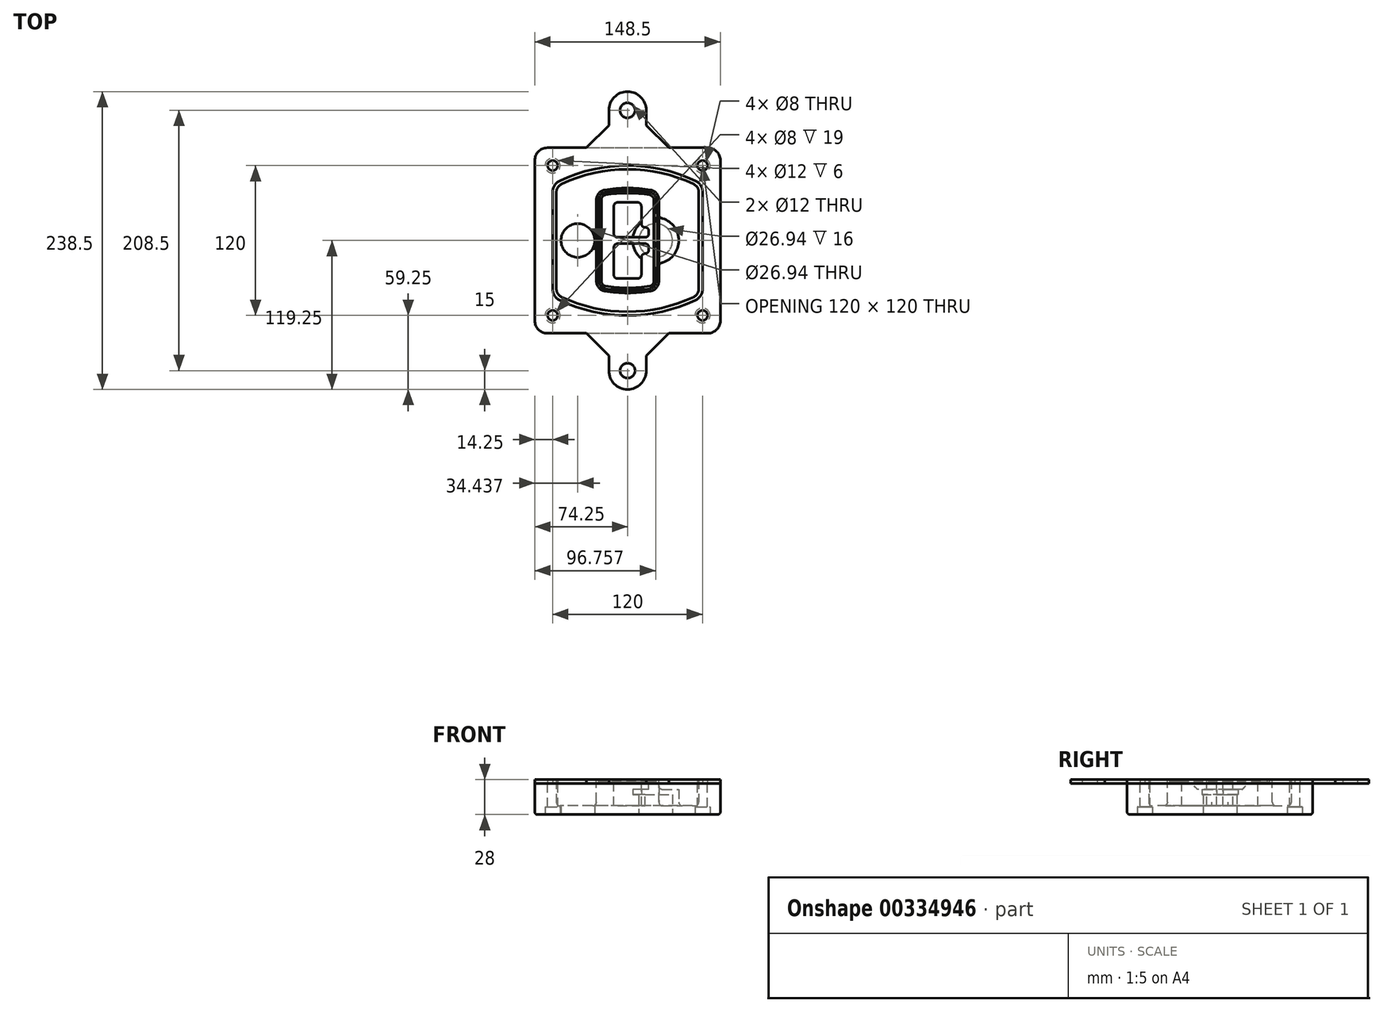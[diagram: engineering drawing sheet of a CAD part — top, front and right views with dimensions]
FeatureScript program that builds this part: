
annotation { "Feature Type Name" : "Feature", "Feature Type Description" : "" }
export const myFeature = defineFeature(function(context is Context, id is Id, definition is map)
    precondition{}
    {
        {
            var Q0;
            Q0=qCreatedBy(makeId("Top.planeOp"),FACE);
            var sketch = newSketch(context, id + "F0", { "sketchPlane" : qUnion([Q0])});
            skPoint(sketch, "E0.rect.middle", {"position": v(0, 0) * mm});
            skLineSegment(sketch, "E1.bottom", {"start": v(-64.25, -74.25) * mm, "end": v(64.25, -74.25) * mm});
            skLineSegment(sketch, "E1.top", {"start": v(-64.25, 74.25) * mm, "end": v(64.25, 74.25) * mm});
            skLineSegment(sketch, "E1.left", {"start": v(-74.25, -64.25) * mm, "end": v(-74.25, 64.25) * mm});
            skLineSegment(sketch, "E1.right", {"start": v(74.25, -64.25) * mm, "end": v(74.25, 64.25) * mm});
            skLineSegment(sketch, "E2", {"start": v(-74.25, 74.25) * mm, "end": v(74.25, -74.25) * mm, "construction": true});
            skLineSegment(sketch, "E3", {"start": v(74.25, 74.25) * mm, "end": v(-74.25, -74.25) * mm, "construction": true});
            skCircle(sketch, "E4", {"center": v(-60, 60) * mm, "radius": 4 * mm});
            skCircle(sketch, "E5", {"center": v(60, 60) * mm, "radius": 4 * mm});
            skCircle(sketch, "E6", {"center": v(60, -60) * mm, "radius": 4 * mm});
            skCircle(sketch, "E7", {"center": v(-60, -60) * mm, "radius": 4 * mm});
            skLineSegment(sketch, "E8", {"start": v(-60, 60) * mm, "end": v(60, 60) * mm, "construction": true});
            skLineSegment(sketch, "E9", {"start": v(60, 60) * mm, "end": v(60, -60) * mm, "construction": true});
            skLineSegment(sketch, "E10", {"start": v(60, -60) * mm, "end": v(-60, -60) * mm, "construction": true});
            skLineSegment(sketch, "E11", {"start": v(-60, -60) * mm, "end": v(-60, 60) * mm, "construction": true});
            skLineSegment(sketch, "E12", {"start": v(-60, 38.83) * mm, "end": v(-60, -38.83) * mm});
            skLineSegment(sketch, "E13", {"start": v(60, 38.83) * mm, "end": v(60, -38.83) * mm});
            skArc(sketch, "E14", {"start": v(54.26, 47.88) * mm, "mid": v(0, 60) * mm, "end": v(-54.26, 47.88) * mm});
            skArc(sketch, "E15", {"start": v(-54.26, -47.88) * mm, "mid": v(0, -60) * mm, "end": v(54.26, -47.88) * mm});
            skLineSegment(sketch, "E16", {"start": v(-60, 0) * mm, "end": v(60, 0) * mm, "construction": true});
            skPoint(sketch, "E17.visualSharp", {"position": v(-60, -45) * mm});
            skArc(sketch, "E17.filletArc", {"start": v(-60, -38.83) * mm, "mid": v(-58.44, -44.2) * mm, "end": v(-54.26, -47.88) * mm});
            skPoint(sketch, "E18.visualSharp", {"position": v(-60, 45) * mm});
            skArc(sketch, "E18.filletArc", {"start": v(-54.26, 47.88) * mm, "mid": v(-58.44, 44.2) * mm, "end": v(-60, 38.83) * mm});
            skPoint(sketch, "E19.visualSharp", {"position": v(60, 45) * mm});
            skArc(sketch, "E19.filletArc", {"start": v(60, 38.83) * mm, "mid": v(58.44, 44.2) * mm, "end": v(54.26, 47.88) * mm});
            skPoint(sketch, "E20.visualSharp", {"position": v(60, -45) * mm});
            skArc(sketch, "E20.filletArc", {"start": v(54.26, -47.88) * mm, "mid": v(58.44, -44.2) * mm, "end": v(60, -38.83) * mm});
            skPoint(sketch, "E21.visualSharp", {"position": v(-74.25, 74.25) * mm});
            skArc(sketch, "E21.filletArc", {"start": v(-64.25, 74.25) * mm, "mid": v(-71.32, 71.32) * mm, "end": v(-74.25, 64.25) * mm});
            skPoint(sketch, "E22.visualSharp", {"position": v(74.25, 74.25) * mm});
            skArc(sketch, "E22.filletArc", {"start": v(74.25, 64.25) * mm, "mid": v(71.32, 71.32) * mm, "end": v(64.25, 74.25) * mm});
            skPoint(sketch, "E23.visualSharp", {"position": v(74.25, -74.25) * mm});
            skArc(sketch, "E23.filletArc", {"start": v(64.25, -74.25) * mm, "mid": v(71.32, -71.32) * mm, "end": v(74.25, -64.25) * mm});
            skPoint(sketch, "E24.visualSharp", {"position": v(-74.25, -74.25) * mm});
            skArc(sketch, "E24.filletArc", {"start": v(-74.25, -64.25) * mm, "mid": v(-71.32, -71.32) * mm, "end": v(-64.25, -74.25) * mm});
            skArc(sketch, "E25.0", {"start": v(57, 38.83) * mm, "mid": v(55.9, 42.58) * mm, "end": v(52.98, 45.17) * mm});
            skLineSegment(sketch, "E25.1", {"start": v(57, 38.83) * mm, "end": v(57, -38.83) * mm});
            skArc(sketch, "E25.2", {"start": v(52.98, -45.17) * mm, "mid": v(55.9, -42.58) * mm, "end": v(57, -38.83) * mm});
            skArc(sketch, "E25.3", {"start": v(-52.98, -45.17) * mm, "mid": v(0, -57) * mm, "end": v(52.98, -45.17) * mm});
            skArc(sketch, "E25.4", {"start": v(-57, -38.83) * mm, "mid": v(-55.9, -42.58) * mm, "end": v(-52.98, -45.17) * mm});
            skArc(sketch, "E25.5", {"start": v(52.98, 45.17) * mm, "mid": v(0, 57) * mm, "end": v(-52.98, 45.17) * mm});
            skLineSegment(sketch, "E25.6", {"start": v(-57, 38.83) * mm, "end": v(-57, -38.83) * mm});
            skArc(sketch, "E25.7", {"start": v(-52.98, 45.17) * mm, "mid": v(-55.9, 42.58) * mm, "end": v(-57, 38.83) * mm});
            skArc(sketch, "E26.0", {"start": v(-55.96, 51.5) * mm, "mid": v(-61.82, 46.33) * mm, "end": v(-64, 38.83) * mm});
            skArc(sketch, "E26.1", {"start": v(55.96, 51.5) * mm, "mid": v(0, 64) * mm, "end": v(-55.96, 51.5) * mm});
            skArc(sketch, "E26.2", {"start": v(64, 38.83) * mm, "mid": v(61.82, 46.33) * mm, "end": v(55.96, 51.5) * mm});
            skLineSegment(sketch, "E26.3", {"start": v(64, 38.83) * mm, "end": v(64, -38.83) * mm});
            skArc(sketch, "E26.4", {"start": v(55.96, -51.5) * mm, "mid": v(61.82, -46.33) * mm, "end": v(64, -38.83) * mm});
            skLineSegment(sketch, "E26.5", {"start": v(-64, 38.83) * mm, "end": v(-64, -38.83) * mm});
            skArc(sketch, "E26.6", {"start": v(-55.96, -51.5) * mm, "mid": v(0, -64) * mm, "end": v(55.96, -51.5) * mm});
            skArc(sketch, "E26.7", {"start": v(-64, -38.83) * mm, "mid": v(-61.82, -46.33) * mm, "end": v(-55.96, -51.5) * mm});
            skSolve(sketch);
        }
        {
            var Q0;
            Q0=makeQuery(id+"F0.imprint","IMPRINT",FACE,{"disambiguationData":[TD([[makeQuery(id+"F0.imprint","IMPRINT",EDGE,{"derivedFrom":sQuery(id+"F0.wireOp",EDGE,"E1.bottom")}),1.0]])]});
            var Q1;
            Q1=makeQuery(id+"F0.imprint","IMPRINT",FACE,{"disambiguationData":[TD([[makeQuery(id+"F0.imprint","IMPRINT",EDGE,{"derivedFrom":sQuery(id+"F0.wireOp",EDGE,"E12")}),1.0]])]});
            var Q2;
            Q2=makeQuery(id+"F0.imprint","IMPRINT",FACE,{"disambiguationData":[TD([[makeQuery(id+"F0.imprint","IMPRINT",EDGE,{"derivedFrom":sQuery(id+"F0.wireOp",EDGE,"E25.0")}),1.0]])]});
            var Q3;
            Q3=makeQuery(id+"F0.imprint","IMPRINT",FACE,{"disambiguationData":[TD([[makeQuery(id+"F0.imprint","IMPRINT",EDGE,{"derivedFrom":sQuery(id+"F0.wireOp",EDGE,"E12")}),-1.0]])]});
            extrude(context, id + "F1", {"entities" : qUnion([Q0, Q1, Q2, Q3]), "oppositeDirection" : true, "depth" : 25 * mm});
        }
        {
            var Q0;
            Q0=makeQuery(id+"F0.imprint","IMPRINT",FACE,{"disambiguationData":[TD([[makeQuery(id+"F0.imprint","IMPRINT",EDGE,{"derivedFrom":sQuery(id+"F0.wireOp",EDGE,"E12")}),1.0]])]});
            extrude(context, id + "F2", {"entities" : qUnion([Q0]), "operationType" : NewBodyOperationType.ADD, "depth" : 3 * mm});
        }
        {
            var Q0;
            Q0=makeQuery(id+"F0.imprint","IMPRINT",FACE,{"disambiguationData":[TD([[makeQuery(id+"F0.imprint","IMPRINT",EDGE,{"derivedFrom":sQuery(id+"F0.wireOp",EDGE,"E25.0")}),1.0]])]});
            extrude(context, id + "F3", {"entities" : qUnion([Q0]), "operationType" : NewBodyOperationType.REMOVE, "oppositeDirection" : true, "depth" : 18 * mm});
        }
        {
            var Q0;
            Q0=makeQuery(id+"F2.opExtrude","CAP_FACE",FACE,{"disambiguationData":[OSD([sQuery(id+"F0.wireOp",EDGE,"E12"),sQuery(id+"F0.wireOp",EDGE,"E13"),sQuery(id+"F0.wireOp",EDGE,"E14"),sQuery(id+"F0.wireOp",EDGE,"E15"),sQuery(id+"F0.wireOp",EDGE,"E17.filletArc"),sQuery(id+"F0.wireOp",EDGE,"E18.filletArc"),sQuery(id+"F0.wireOp",EDGE,"E19.filletArc"),sQuery(id+"F0.wireOp",EDGE,"E20.filletArc"),sQuery(id+"F0.wireOp",EDGE,"E25.0"),sQuery(id+"F0.wireOp",EDGE,"E25.1"),sQuery(id+"F0.wireOp",EDGE,"E25.2"),sQuery(id+"F0.wireOp",EDGE,"E25.3"),sQuery(id+"F0.wireOp",EDGE,"E25.4"),sQuery(id+"F0.wireOp",EDGE,"E25.5"),sQuery(id+"F0.wireOp",EDGE,"E25.6"),sQuery(id+"F0.wireOp",EDGE,"E25.7")])],"isStart":false});
            var sketch = newSketch(context, id + "F4", { "sketchPlane" : qUnion([Q0])});
            skArc(sketch, "E27.0", {"start": v(-18.34, -40.45) * mm, "mid": v(0, -42) * mm, "end": v(18.34, -40.45) * mm});
            skArc(sketch, "E28.0", {"start": v(18.34, 40.45) * mm, "mid": v(0, 42) * mm, "end": v(-18.34, 40.45) * mm});
            skLineSegment(sketch, "E29", {"start": v(-25, 32.57) * mm, "end": v(-25, -32.57) * mm});
            skLineSegment(sketch, "E30", {"start": v(25, 32.57) * mm, "end": v(25, -32.57) * mm});
            skLineSegment(sketch, "E31", {"start": v(-25, 39.1) * mm, "end": v(25, 39.1) * mm, "construction": true});
            skLineSegment(sketch, "E32", {"start": v(-25, -39.1) * mm, "end": v(25, -39.1) * mm, "construction": true});
            skPoint(sketch, "E33.visualSharp", {"position": v(-25, 39.1) * mm});
            skArc(sketch, "E33.filletArc", {"start": v(-18.34, 40.45) * mm, "mid": v(-23.11, 37.73) * mm, "end": v(-25, 32.57) * mm});
            skPoint(sketch, "E34.visualSharp", {"position": v(25, 39.1) * mm});
            skArc(sketch, "E34.filletArc", {"start": v(25, 32.57) * mm, "mid": v(23.11, 37.73) * mm, "end": v(18.34, 40.45) * mm});
            skPoint(sketch, "E35.visualSharp", {"position": v(25, -39.1) * mm});
            skArc(sketch, "E35.filletArc", {"start": v(18.34, -40.45) * mm, "mid": v(23.11, -37.73) * mm, "end": v(25, -32.57) * mm});
            skPoint(sketch, "E36.visualSharp", {"position": v(-25, -39.1) * mm});
            skArc(sketch, "E36.filletArc", {"start": v(-25, -32.57) * mm, "mid": v(-23.11, -37.73) * mm, "end": v(-18.34, -40.45) * mm});
            skArc(sketch, "E37.0", {"start": v(52.98, 45.17) * mm, "mid": v(0, 57) * mm, "end": v(-52.98, 45.17) * mm});
            skArc(sketch, "E37.1", {"start": v(-52.98, 45.17) * mm, "mid": v(-55.9, 42.58) * mm, "end": v(-57, 38.83) * mm});
            skLineSegment(sketch, "E37.2", {"start": v(-57, 38.83) * mm, "end": v(-57, -38.83) * mm});
            skArc(sketch, "E37.3", {"start": v(-57, -38.83) * mm, "mid": v(-55.9, -42.58) * mm, "end": v(-52.98, -45.17) * mm});
            skArc(sketch, "E37.4", {"start": v(-52.98, -45.17) * mm, "mid": v(0, -57) * mm, "end": v(52.98, -45.17) * mm});
            skArc(sketch, "E37.5", {"start": v(52.98, -45.17) * mm, "mid": v(55.9, -42.58) * mm, "end": v(57, -38.83) * mm});
            skLineSegment(sketch, "E37.6", {"start": v(57, 38.83) * mm, "end": v(57, -38.83) * mm});
            skArc(sketch, "E37.7", {"start": v(57, 38.83) * mm, "mid": v(55.9, 42.58) * mm, "end": v(52.98, 45.17) * mm});
            skLineSegment(sketch, "E38.0", {"start": v(23, 32.57) * mm, "end": v(23, -32.57) * mm});
            skArc(sketch, "E38.1", {"start": v(18, -38.48) * mm, "mid": v(21.58, -36.44) * mm, "end": v(23, -32.57) * mm});
            skArc(sketch, "E38.2", {"start": v(-18, -38.48) * mm, "mid": v(0, -40) * mm, "end": v(18, -38.48) * mm});
            skArc(sketch, "E38.3", {"start": v(-23, -32.57) * mm, "mid": v(-21.58, -36.44) * mm, "end": v(-18, -38.48) * mm});
            skLineSegment(sketch, "E38.4", {"start": v(-23, 32.57) * mm, "end": v(-23, -32.57) * mm});
            skArc(sketch, "E38.5", {"start": v(23, 32.57) * mm, "mid": v(21.58, 36.44) * mm, "end": v(18, 38.48) * mm});
            skArc(sketch, "E38.6", {"start": v(-18, 38.48) * mm, "mid": v(-21.58, 36.44) * mm, "end": v(-23, 32.57) * mm});
            skArc(sketch, "E38.7", {"start": v(18, 38.48) * mm, "mid": v(0, 40) * mm, "end": v(-18, 38.48) * mm});
            skArc(sketch, "E39.0", {"start": v(21, 32.57) * mm, "mid": v(20.06, 35.15) * mm, "end": v(17.67, 36.5) * mm});
            skLineSegment(sketch, "E39.1", {"start": v(21, 32.57) * mm, "end": v(21, -32.57) * mm});
            skArc(sketch, "E39.2", {"start": v(17.67, -36.5) * mm, "mid": v(20.06, -35.15) * mm, "end": v(21, -32.57) * mm});
            skArc(sketch, "E39.3", {"start": v(-17.67, -36.5) * mm, "mid": v(0, -38) * mm, "end": v(17.67, -36.5) * mm});
            skArc(sketch, "E39.4", {"start": v(-21, -32.57) * mm, "mid": v(-20.06, -35.15) * mm, "end": v(-17.67, -36.5) * mm});
            skArc(sketch, "E39.5", {"start": v(17.67, 36.5) * mm, "mid": v(0, 38) * mm, "end": v(-17.67, 36.5) * mm});
            skLineSegment(sketch, "E39.6", {"start": v(-21, 32.57) * mm, "end": v(-21, -32.57) * mm});
            skArc(sketch, "E39.7", {"start": v(-17.67, 36.5) * mm, "mid": v(-20.06, 35.15) * mm, "end": v(-21, 32.57) * mm});
            skLineSegment(sketch, "E40", {"start": v(-25, 0) * mm, "end": v(25, 0) * mm, "construction": true});
            skLineSegment(sketch, "E41", {"start": v(-11, 5.5) * mm, "end": v(-11, 27.5) * mm});
            skLineSegment(sketch, "E42", {"start": v(-8, 30.5) * mm, "end": v(8, 30.5) * mm});
            skLineSegment(sketch, "E43", {"start": v(11, 27.5) * mm, "end": v(11, 13.5) * mm});
            skLineSegment(sketch, "E44", {"start": v(14, 10.5) * mm, "end": v(14, 10.5) * mm});
            skLineSegment(sketch, "E45", {"start": v(17, 7.5) * mm, "end": v(17, 5.5) * mm});
            skLineSegment(sketch, "E46", {"start": v(14, 2.5) * mm, "end": v(-8, 2.5) * mm});
            skPoint(sketch, "E47.visualSharp", {"position": v(-11, 30.5) * mm});
            skArc(sketch, "E47.filletArc", {"start": v(-8, 30.5) * mm, "mid": v(-10.12, 29.62) * mm, "end": v(-11, 27.5) * mm});
            skPoint(sketch, "E48.visualSharp", {"position": v(11, 30.5) * mm});
            skArc(sketch, "E48.filletArc", {"start": v(11, 27.5) * mm, "mid": v(10.12, 29.62) * mm, "end": v(8, 30.5) * mm});
            skPoint(sketch, "E49.visualSharp", {"position": v(11, 10.5) * mm});
            skArc(sketch, "E49.filletArc", {"start": v(11, 13.5) * mm, "mid": v(11.88, 11.38) * mm, "end": v(14, 10.5) * mm});
            skPoint(sketch, "E50.visualSharp", {"position": v(17, 10.5) * mm});
            skArc(sketch, "E50.filletArc", {"start": v(17, 7.5) * mm, "mid": v(16.12, 9.62) * mm, "end": v(14, 10.5) * mm});
            skPoint(sketch, "E51.visualSharp", {"position": v(17, 2.5) * mm});
            skArc(sketch, "E51.filletArc", {"start": v(14, 2.5) * mm, "mid": v(16.12, 3.38) * mm, "end": v(17, 5.5) * mm});
            skPoint(sketch, "E52.visualSharp", {"position": v(-11, 2.5) * mm});
            skArc(sketch, "E52.filletArc", {"start": v(-11, 5.5) * mm, "mid": v(-10.12, 3.38) * mm, "end": v(-8, 2.5) * mm});
            skLineSegment(sketch, "E53.0.MirrorCS", {"start": v(14, -2.5) * mm, "end": v(-8, -2.5) * mm});
            skArc(sketch, "E54.0.MirrorCS", {"start": v(-11, -5.5) * mm, "mid": v(-10.12, -3.38) * mm, "end": v(-8, -2.5) * mm});
            skLineSegment(sketch, "E55.0.MirrorCS", {"start": v(-11, -5.5) * mm, "end": v(-11, -27.5) * mm});
            skArc(sketch, "E56.0.MirrorCS", {"start": v(-8, -30.5) * mm, "mid": v(-10.12, -29.62) * mm, "end": v(-11, -27.5) * mm});
            skLineSegment(sketch, "E57.0.MirrorCS", {"start": v(-8, -30.5) * mm, "end": v(8, -30.5) * mm});
            skArc(sketch, "E58.0.MirrorCS", {"start": v(11, -27.5) * mm, "mid": v(10.12, -29.62) * mm, "end": v(8, -30.5) * mm});
            skLineSegment(sketch, "E59.0.MirrorCS", {"start": v(11, -27.5) * mm, "end": v(11, -13.5) * mm});
            skArc(sketch, "E60.0.MirrorCS", {"start": v(11, -13.5) * mm, "mid": v(11.88, -11.38) * mm, "end": v(14, -10.5) * mm});
            skArc(sketch, "E61.0.MirrorCS", {"start": v(17, -7.5) * mm, "mid": v(16.12, -9.62) * mm, "end": v(14, -10.5) * mm});
            skLineSegment(sketch, "E62.0.MirrorCS", {"start": v(17, -7.5) * mm, "end": v(17, -5.5) * mm});
            skArc(sketch, "E63.0.MirrorCS", {"start": v(14, -2.5) * mm, "mid": v(16.12, -3.38) * mm, "end": v(17, -5.5) * mm});
            skSolve(sketch);
        }
        {
            var Q0;
            Q0=makeQuery(id+"F4.imprint","IMPRINT",FACE,{"disambiguationData":[TD([[makeQuery(id+"F4.imprint","IMPRINT",EDGE,{"derivedFrom":sQuery(id+"F4.wireOp",EDGE,"E27.0")}),1.0]])]});
            var Q1;
            Q1=makeQuery(id+"F4.imprint","IMPRINT",FACE,{"disambiguationData":[TD([[makeQuery(id+"F4.imprint","IMPRINT",EDGE,{"derivedFrom":sQuery(id+"F4.wireOp",EDGE,"E38.0")}),-1.0]])]});
            var Q2;
            Q2=makeQuery(id+"F4.imprint","IMPRINT",FACE,{"disambiguationData":[TD([[makeQuery(id+"F4.imprint","IMPRINT",EDGE,{"derivedFrom":sQuery(id+"F4.wireOp",EDGE,"E39.0")}),1.0]])]});
            extrude(context, id + "F5", {"entities" : qUnion([Q0, Q1, Q2]), "operationType" : NewBodyOperationType.ADD, "endBound" : BoundingType.UP_TO_NEXT, "oppositeDirection" : true, "depth" : 25 * mm});
        }
        {
            var Q0;
            Q0=makeQuery(id+"F4.imprint","IMPRINT",FACE,{"disambiguationData":[TD([[makeQuery(id+"F4.imprint","IMPRINT",EDGE,{"derivedFrom":sQuery(id+"F4.wireOp",EDGE,"E38.0")}),-1.0]])]});
            extrude(context, id + "F6", {"entities" : qUnion([Q0]), "operationType" : NewBodyOperationType.REMOVE, "oppositeDirection" : true, "depth" : 2 * mm});
        }
        {
            var Q0;
            Q0=makeQuery(id+"F1.opExtrude","CAP_FACE",FACE,{"disambiguationData":[OSD([sQuery(id+"F0.wireOp",EDGE,"E1.bottom"),sQuery(id+"F0.wireOp",EDGE,"E1.top"),sQuery(id+"F0.wireOp",EDGE,"E1.left"),sQuery(id+"F0.wireOp",EDGE,"E1.right"),sQuery(id+"F0.wireOp",EDGE,"E4"),sQuery(id+"F0.wireOp",EDGE,"E5"),sQuery(id+"F0.wireOp",EDGE,"E6"),sQuery(id+"F0.wireOp",EDGE,"E7"),sQuery(id+"F0.wireOp",EDGE,"E21.filletArc"),sQuery(id+"F0.wireOp",EDGE,"E22.filletArc"),sQuery(id+"F0.wireOp",EDGE,"E23.filletArc"),sQuery(id+"F0.wireOp",EDGE,"E24.filletArc")])],"isStart":false});
            var sketch = newSketch(context, id + "F7", { "sketchPlane" : qUnion([Q0])});
            skCircle(sketch, "E64", {"center": v(22.5, 0) * mm, "radius": 13.47 * mm});
            skCircle(sketch, "E65", {"center": v(-39.81, 0) * mm, "radius": 13.47 * mm});
            skLineSegment(sketch, "E66", {"start": v(74.25, 0) * mm, "end": v(-74.25, 0) * mm});
            skCircle(sketch, "E67", {"center": v(22.5, 0) * mm, "radius": 18.47 * mm});
            skCircle(sketch, "E68", {"center": v(60, -60) * mm, "radius": 6 * mm});
            skCircle(sketch, "E69", {"center": v(-60, -60) * mm, "radius": 6 * mm});
            skCircle(sketch, "E70", {"center": v(-60, 60) * mm, "radius": 6 * mm});
            skCircle(sketch, "E71", {"center": v(60, 60) * mm, "radius": 6 * mm});
            skSolve(sketch);
        }
        {
            var Q0;
            {var subQ1=sQuery(id+"F7.wireOp",EDGE,"E66");var subQ4=sQuery(id+"F7.wireOp",EDGE,"E64");var subQ6=makeQuery(id+"F7.imprint","INTERSECT",VERTEX,{"disambiguationData":[OD(0.0)],"derivedFrom":[subQ4,subQ1]});Q0=makeQuery(id+"F7.imprint","IMPRINT",FACE,{"disambiguationData":[TD([[makeQuery(id+"F7.imprint","IMPRINT",EDGE,{"disambiguationData":[TD([[subQ6,-1.0]])],"derivedFrom":subQ4}),-1.0]])]});}
            var Q1;
            {var subQ0=sQuery(id+"F7.wireOp",EDGE,"E66");var subQ1=sQuery(id+"F7.wireOp",EDGE,"E64");var subQ3=makeQuery(id+"F7.imprint","INTERSECT",VERTEX,{"disambiguationData":[OD(0.0)],"derivedFrom":[subQ1,subQ0]});Q1=makeQuery(id+"F7.imprint","IMPRINT",FACE,{"disambiguationData":[TD([[makeQuery(id+"F7.imprint","IMPRINT",EDGE,{"disambiguationData":[TD([[subQ3,-1.0]])],"derivedFrom":subQ1}),1.0]])]});}
            var Q2;
            {var subQ0=sQuery(id+"F7.wireOp",EDGE,"E66");var subQ1=sQuery(id+"F7.wireOp",EDGE,"E64");var subQ3=makeQuery(id+"F7.imprint","INTERSECT",VERTEX,{"disambiguationData":[OD(0.0)],"derivedFrom":[subQ1,subQ0]});Q2=makeQuery(id+"F7.imprint","IMPRINT",FACE,{"disambiguationData":[TD([[makeQuery(id+"F7.imprint","IMPRINT",EDGE,{"disambiguationData":[TD([[subQ3,1.0]])],"derivedFrom":subQ1}),1.0]])]});}
            var Q3;
            {var subQ1=sQuery(id+"F7.wireOp",EDGE,"E66");var subQ4=sQuery(id+"F7.wireOp",EDGE,"E64");var subQ6=makeQuery(id+"F7.imprint","INTERSECT",VERTEX,{"disambiguationData":[OD(0.0)],"derivedFrom":[subQ4,subQ1]});Q3=makeQuery(id+"F7.imprint","IMPRINT",FACE,{"disambiguationData":[TD([[makeQuery(id+"F7.imprint","IMPRINT",EDGE,{"disambiguationData":[TD([[subQ6,1.0]])],"derivedFrom":subQ4}),-1.0]])]});}
            extrude(context, id + "F8", {"entities" : qUnion([Q0, Q1, Q2, Q3]), "operationType" : NewBodyOperationType.ADD, "oppositeDirection" : true, "depth" : 20 * mm});
        }
        {
            var Q0;
            {var subQ0=sQuery(id+"F7.wireOp",EDGE,"E66");var subQ1=sQuery(id+"F7.wireOp",EDGE,"E64");var subQ3=makeQuery(id+"F7.imprint","INTERSECT",VERTEX,{"disambiguationData":[OD(0.0)],"derivedFrom":[subQ1,subQ0]});Q0=makeQuery(id+"F7.imprint","IMPRINT",FACE,{"disambiguationData":[TD([[makeQuery(id+"F7.imprint","IMPRINT",EDGE,{"disambiguationData":[TD([[subQ3,-1.0]])],"derivedFrom":subQ1}),1.0]])]});}
            var Q1;
            {var subQ0=sQuery(id+"F7.wireOp",EDGE,"E66");var subQ1=sQuery(id+"F7.wireOp",EDGE,"E64");var subQ3=makeQuery(id+"F7.imprint","INTERSECT",VERTEX,{"disambiguationData":[OD(0.0)],"derivedFrom":[subQ1,subQ0]});Q1=makeQuery(id+"F7.imprint","IMPRINT",FACE,{"disambiguationData":[TD([[makeQuery(id+"F7.imprint","IMPRINT",EDGE,{"disambiguationData":[TD([[subQ3,1.0]])],"derivedFrom":subQ1}),1.0]])]});}
            extrude(context, id + "F9", {"entities" : qUnion([Q0, Q1]), "operationType" : NewBodyOperationType.REMOVE, "oppositeDirection" : true, "depth" : 16 * mm});
        }
        {
            var Q0;
            {var subQ0=sQuery(id+"F7.wireOp",EDGE,"E66");var subQ1=sQuery(id+"F7.wireOp",EDGE,"E65");var subQ3=makeQuery(id+"F7.imprint","INTERSECT",VERTEX,{"disambiguationData":[OD(0.0)],"derivedFrom":[subQ1,subQ0]});Q0=makeQuery(id+"F7.imprint","IMPRINT",FACE,{"disambiguationData":[TD([[makeQuery(id+"F7.imprint","IMPRINT",EDGE,{"disambiguationData":[TD([[subQ3,-1.0]])],"derivedFrom":subQ1}),1.0]])]});}
            var Q1;
            {var subQ0=sQuery(id+"F7.wireOp",EDGE,"E66");var subQ1=sQuery(id+"F7.wireOp",EDGE,"E65");var subQ3=makeQuery(id+"F7.imprint","INTERSECT",VERTEX,{"disambiguationData":[OD(0.0)],"derivedFrom":[subQ1,subQ0]});Q1=makeQuery(id+"F7.imprint","IMPRINT",FACE,{"disambiguationData":[TD([[makeQuery(id+"F7.imprint","IMPRINT",EDGE,{"disambiguationData":[TD([[subQ3,1.0]])],"derivedFrom":subQ1}),1.0]])]});}
            extrude(context, id + "F10", {"entities" : qUnion([Q0, Q1]), "operationType" : NewBodyOperationType.REMOVE, "oppositeDirection" : true, "depth" : 25 * mm});
        }
        {
            var Q0;
            Q0=makeQuery(id+"F7.imprint","IMPRINT",FACE,{"disambiguationData":[TD([[makeQuery(id+"F7.imprint","IMPRINT",EDGE,{"derivedFrom":sQuery(id+"F7.wireOp",EDGE,"E68")}),1.0]])]});
            var Q1;
            Q1=makeQuery(id+"F7.imprint","IMPRINT",FACE,{"disambiguationData":[TD([[makeQuery(id+"F7.imprint","IMPRINT",EDGE,{"derivedFrom":makeQuery(id+"F1.opExtrude","CAP_EDGE",EDGE,{"disambiguationData":[OSD([sQuery(id+"F0.wireOp",EDGE,"E5")])],"isStart":false})}),-1.0]])]});
            var Q2;
            Q2=makeQuery(id+"F7.imprint","IMPRINT",FACE,{"disambiguationData":[TD([[makeQuery(id+"F7.imprint","IMPRINT",EDGE,{"derivedFrom":sQuery(id+"F7.wireOp",EDGE,"E69")}),1.0]])]});
            var Q3;
            Q3=makeQuery(id+"F7.imprint","IMPRINT",FACE,{"disambiguationData":[TD([[makeQuery(id+"F7.imprint","IMPRINT",EDGE,{"derivedFrom":makeQuery(id+"F1.opExtrude","CAP_EDGE",EDGE,{"disambiguationData":[OSD([sQuery(id+"F0.wireOp",EDGE,"E4")])],"isStart":false})}),-1.0]])]});
            var Q4;
            Q4=makeQuery(id+"F7.imprint","IMPRINT",FACE,{"disambiguationData":[TD([[makeQuery(id+"F7.imprint","IMPRINT",EDGE,{"derivedFrom":sQuery(id+"F7.wireOp",EDGE,"E70")}),1.0]])]});
            var Q5;
            Q5=makeQuery(id+"F7.imprint","IMPRINT",FACE,{"disambiguationData":[TD([[makeQuery(id+"F7.imprint","IMPRINT",EDGE,{"derivedFrom":makeQuery(id+"F1.opExtrude","CAP_EDGE",EDGE,{"disambiguationData":[OSD([sQuery(id+"F0.wireOp",EDGE,"E7")])],"isStart":false})}),-1.0]])]});
            var Q6;
            Q6=makeQuery(id+"F7.imprint","IMPRINT",FACE,{"disambiguationData":[TD([[makeQuery(id+"F7.imprint","IMPRINT",EDGE,{"derivedFrom":sQuery(id+"F7.wireOp",EDGE,"E71")}),1.0]])]});
            var Q7;
            Q7=makeQuery(id+"F7.imprint","IMPRINT",FACE,{"disambiguationData":[TD([[makeQuery(id+"F7.imprint","IMPRINT",EDGE,{"derivedFrom":makeQuery(id+"F1.opExtrude","CAP_EDGE",EDGE,{"disambiguationData":[OSD([sQuery(id+"F0.wireOp",EDGE,"E6")])],"isStart":false})}),-1.0]])]});
            extrude(context, id + "F11", {"entities" : qUnion([Q0, Q1, Q2, Q3, Q4, Q5, Q6, Q7]), "operationType" : NewBodyOperationType.REMOVE, "oppositeDirection" : true, "depth" : 6 * mm});
        }
        {
            var Q0;
            Q0=makeQuery(id+"F9.boolean.opBoolean","COPY",FACE,{"derivedFrom":makeQuery(id+"F9.opExtrude","CAP_FACE",FACE,{"disambiguationData":[OSD([sQuery(id+"F7.wireOp",EDGE,"E64")])],"isStart":false})});
            var sketch = newSketch(context, id + "F12", { "sketchPlane" : qUnion([Q0])});
            skArc(sketch, "E72.0", {"start": v(11, 14.45) * mm, "mid": v(6.45, 9.13) * mm, "end": v(4.2, 2.5) * mm});
            skArc(sketch, "E72.1", {"start": v(4.2, -2.5) * mm, "mid": v(6.45, -9.13) * mm, "end": v(11, -14.45) * mm});
            skLineSegment(sketch, "E73", {"start": v(4.2, -2.5) * mm, "end": v(14, -2.5) * mm});
            skLineSegment(sketch, "E74.0", {"start": v(14, 2.5) * mm, "end": v(4.2, 2.5) * mm});
            skArc(sketch, "E74.1", {"start": v(14, 2.5) * mm, "mid": v(16.12, 3.38) * mm, "end": v(17, 5.5) * mm});
            skLineSegment(sketch, "E74.2", {"start": v(17, 7.5) * mm, "end": v(17, 5.5) * mm});
            skArc(sketch, "E74.3", {"start": v(17, 7.5) * mm, "mid": v(16.12, 9.62) * mm, "end": v(14, 10.5) * mm});
            skArc(sketch, "E74.4", {"start": v(11, 13.5) * mm, "mid": v(11.88, 11.38) * mm, "end": v(14, 10.5) * mm});
            skLineSegment(sketch, "E74.5", {"start": v(11, 14.45) * mm, "end": v(11, 13.5) * mm});
            skLineSegment(sketch, "E74.7", {"start": v(14, -2.5) * mm, "end": v(4.2, -2.5) * mm});
            skArc(sketch, "E74.8", {"start": v(14, -2.5) * mm, "mid": v(16.12, -3.38) * mm, "end": v(17, -5.5) * mm});
            skLineSegment(sketch, "E74.9", {"start": v(17, -7.5) * mm, "end": v(17, -5.5) * mm});
            skArc(sketch, "E74.10", {"start": v(17, -7.5) * mm, "mid": v(16.12, -9.62) * mm, "end": v(14, -10.5) * mm});
            skArc(sketch, "E74.11", {"start": v(11, -13.5) * mm, "mid": v(11.88, -11.38) * mm, "end": v(14, -10.5) * mm});
            skLineSegment(sketch, "E74.12", {"start": v(11, -14.45) * mm, "end": v(11, -13.5) * mm});
            skPoint(sketch, "E75.orphan", {"position": v(11, -27.5) * mm});
            skPoint(sketch, "E76.orphan", {"position": v(-8, -2.5) * mm});
            skPoint(sketch, "E77.orphan", {"position": v(-8, 2.5) * mm});
            skPoint(sketch, "E78.orphan", {"position": v(11, 27.5) * mm});
            skSolve(sketch);
        }
        {
            var Q0;
            {var subQ7=sQuery(id+"F12.wireOp",EDGE,"E72.0");var subQ14=sQuery(id+"F12.wireOp",EDGE,"E72.1");var subQ16=sQuery(id+"F12.wireOp",EDGE,"E74.1");var subQ18=sQuery(id+"F12.wireOp",EDGE,"E74.8");Q0=qUnion([makeQuery(id+"F12.imprint","IMPRINT",FACE,{"disambiguationData":[TD([[makeQuery(id+"F12.imprint","IMPRINT",EDGE,{"derivedFrom":subQ7}),1.0]])]}),makeQuery(id+"F12.imprint","IMPRINT",FACE,{"disambiguationData":[TD([[makeQuery(id+"F12.imprint","IMPRINT",EDGE,{"derivedFrom":subQ14}),1.0]])]}),makeQuery(id+"F12.imprint","IMPRINT",FACE,{"disambiguationData":[TD([[makeQuery(id+"F12.imprint","IMPRINT",EDGE,{"derivedFrom":subQ16}),1.0]])]}),makeQuery(id+"F12.imprint","IMPRINT",FACE,{"disambiguationData":[TD([[makeQuery(id+"F12.imprint","IMPRINT",EDGE,{"derivedFrom":subQ18}),-1.0]])]})]);}
            var Q1;
            Q1=makeQuery(id+"F5.boolean.opBoolean","SPLIT",FACE,{"disambiguationData":[TD([makeQuery(id+"F5.opExtrude","SWEPT_FACE",FACE,{"disambiguationData":[OSD([sQuery(id+"F4.wireOp",EDGE,"E41")])]})])],"derivedFrom":makeQuery(id+"F3.boolean.opBoolean","COPY",FACE,{"derivedFrom":makeQuery(id+"F3.opExtrude","CAP_FACE",FACE,{"disambiguationData":[OSD([sQuery(id+"F0.wireOp",EDGE,"E25.0"),sQuery(id+"F0.wireOp",EDGE,"E25.1"),sQuery(id+"F0.wireOp",EDGE,"E25.2"),sQuery(id+"F0.wireOp",EDGE,"E25.3"),sQuery(id+"F0.wireOp",EDGE,"E25.4"),sQuery(id+"F0.wireOp",EDGE,"E25.5"),sQuery(id+"F0.wireOp",EDGE,"E25.6"),sQuery(id+"F0.wireOp",EDGE,"E25.7")])],"isStart":false})})});
            extrude(context, id + "F13", {"entities" : qUnion([Q0]), "operationType" : NewBodyOperationType.REMOVE, "endBound" : BoundingType.UP_TO_SURFACE, "endBoundEntityFace" : qUnion([Q1]), "depth" : 25 * mm});
        }
        {
            var Q0;
            Q0=makeQuery(id+"F3.boolean.opBoolean","COPY",EDGE,{"derivedFrom":makeQuery(id+"F3.opExtrude","CAP_EDGE",EDGE,{"disambiguationData":[OSD([sQuery(id+"F0.wireOp",EDGE,"E25.6")])],"isStart":false})});
            var Q1;
            Q1=makeQuery(id+"F8.boolean.opBoolean","INTERSECT",EDGE,{"derivedFrom":[makeQuery(id+"F5.opExtrude","SWEPT_FACE",FACE,{"disambiguationData":[OSD([sQuery(id+"F4.wireOp",EDGE,"E30")])]}),makeQuery(id+"F8.opExtrude","CAP_FACE",FACE,{"disambiguationData":[OSD([sQuery(id+"F7.wireOp",EDGE,"E67")])],"isStart":false})]});
            var Q2;
            Q2=makeQuery(id+"F8.boolean.opBoolean","INTERSECT",EDGE,{"disambiguationData":[OD(1.0)],"derivedFrom":[makeQuery(id+"F5.opExtrude","SWEPT_FACE",FACE,{"disambiguationData":[OSD([sQuery(id+"F4.wireOp",EDGE,"E30")])]}),makeQuery(id+"F8.opExtrude","SWEPT_FACE",FACE,{"disambiguationData":[OSD([sQuery(id+"F7.wireOp",EDGE,"E67")])]})]});
            var Q3;
            {var subQ0=sQuery(id+"F4.wireOp",EDGE,"E30");Q3=makeQuery(id+"F8.boolean.opBoolean","SPLIT",EDGE,{"disambiguationData":[TD([makeQuery(id+"F5.opExtrude","SWEPT_FACE",FACE,{"disambiguationData":[OSD([sQuery(id+"F4.wireOp",EDGE,"E35.filletArc")])]})])],"derivedFrom":makeQuery(id+"F5.opExtrude","CAP_EDGE",EDGE,{"disambiguationData":[OSD([subQ0])],"isStart":false})});}
            var Q4;
            {var subQ0=sQuery(id+"F0.wireOp",EDGE,"E25.7");var subQ1=sQuery(id+"F0.wireOp",EDGE,"E25.1");var subQ2=sQuery(id+"F0.wireOp",EDGE,"E25.6");var subQ3=sQuery(id+"F0.wireOp",EDGE,"E25.5");var subQ4=sQuery(id+"F0.wireOp",EDGE,"E25.4");var subQ5=sQuery(id+"F0.wireOp",EDGE,"E25.0");var subQ6=sQuery(id+"F0.wireOp",EDGE,"E25.2");var subQ7=sQuery(id+"F0.wireOp",EDGE,"E25.3");Q4=makeQuery(id+"F8.boolean.opBoolean","INTERSECT",EDGE,{"derivedFrom":[makeQuery(id+"F5.boolean.opBoolean","SPLIT",FACE,{"disambiguationData":[TD([makeQuery(id+"F2.opExtrude","SWEPT_FACE",FACE,{"disambiguationData":[OSD([subQ5])]})])],"derivedFrom":makeQuery(id+"F3.boolean.opBoolean","COPY",FACE,{"derivedFrom":makeQuery(id+"F3.opExtrude","CAP_FACE",FACE,{"disambiguationData":[OSD([subQ5,subQ1,subQ6,subQ7,subQ4,subQ3,subQ2,subQ0])],"isStart":false})})}),makeQuery(id+"F8.opExtrude","SWEPT_FACE",FACE,{"disambiguationData":[OSD([sQuery(id+"F7.wireOp",EDGE,"E67")])]})]});}
            var Q5;
            Q5=makeQuery(id+"F8.boolean.opBoolean","INTERSECT",EDGE,{"disambiguationData":[OD(0.0)],"derivedFrom":[makeQuery(id+"F5.opExtrude","SWEPT_FACE",FACE,{"disambiguationData":[OSD([sQuery(id+"F4.wireOp",EDGE,"E30")])]}),makeQuery(id+"F8.opExtrude","SWEPT_FACE",FACE,{"disambiguationData":[OSD([sQuery(id+"F7.wireOp",EDGE,"E67")])]})]});
            fillet(context, id + "F14", {"entities" : qUnion([Q0, Q1, Q2, Q3, Q4, Q5]), "radius" : 3 * mm, "tangentPropagation" : true, "allowEdgeOverflow" : false});
        }
        {
            var Q0;
            Q0=makeQuery(id+"F1.opExtrude","CAP_EDGE",EDGE,{"disambiguationData":[OSD([sQuery(id+"F0.wireOp",EDGE,"E1.bottom")])],"isStart":false});
            fillet(context, id + "F15", {"entities" : qUnion([Q0]), "radius" : 2 * mm, "tangentPropagation" : true, "allowEdgeOverflow" : false});
        }
        {
            var Q0;
            {var subQ0=sQuery(id+"F0.wireOp",EDGE,"E21.filletArc");var subQ1=sQuery(id+"F0.wireOp",EDGE,"E7");var subQ2=sQuery(id+"F0.wireOp",EDGE,"E6");var subQ3=sQuery(id+"F0.wireOp",EDGE,"E5");var subQ4=sQuery(id+"F0.wireOp",EDGE,"E4");var subQ5=sQuery(id+"F0.wireOp",EDGE,"E22.filletArc");var subQ6=sQuery(id+"F0.wireOp",EDGE,"E1.bottom");var subQ7=sQuery(id+"F0.wireOp",EDGE,"E1.right");var subQ8=sQuery(id+"F0.wireOp",EDGE,"E1.top");var subQ9=sQuery(id+"F0.wireOp",EDGE,"E1.left");var subQ10=sQuery(id+"F0.wireOp",EDGE,"E23.filletArc");var subQ11=sQuery(id+"F0.wireOp",EDGE,"E24.filletArc");Q0=makeQuery(id+"F2.boolean.opBoolean","SPLIT",FACE,{"disambiguationData":[TD([makeQuery(id+"F1.opExtrude","SWEPT_FACE",FACE,{"disambiguationData":[OSD([subQ6])]})])],"derivedFrom":makeQuery(id+"F1.opExtrude","CAP_FACE",FACE,{"disambiguationData":[OSD([subQ6,subQ8,subQ9,subQ7,subQ4,subQ3,subQ2,subQ1,subQ0,subQ5,subQ10,subQ11])],"isStart":true})});}
            var sketch = newSketch(context, id + "F16", { "sketchPlane" : qUnion([Q0])});
            skLineSegment(sketch, "E79", {"start": v(0, 74.25) * mm, "end": v(0, 104.25) * mm, "construction": true});
            skLineSegment(sketch, "E80", {"start": v(-33, 74.25) * mm, "end": v(-15, 92.25) * mm});
            skLineSegment(sketch, "E81", {"start": v(-15, 92.25) * mm, "end": v(-15, 104.25) * mm});
            skLineSegment(sketch, "E82", {"start": v(33, 74.25) * mm, "end": v(15, 92.25) * mm});
            skLineSegment(sketch, "E83", {"start": v(15, 92.25) * mm, "end": v(15, 104.25) * mm});
            skArc(sketch, "E84", {"start": v(15, 104.25) * mm, "mid": v(0, 119.25) * mm, "end": v(-15, 104.25) * mm});
            skCircle(sketch, "E85", {"center": v(0, 104.25) * mm, "radius": 6 * mm});
            skLineSegment(sketch, "E86", {"start": v(-74.25, 0) * mm, "end": v(74.25, 0) * mm, "construction": true});
            skLineSegment(sketch, "E87.MirrorCS", {"start": v(-33, -74.25) * mm, "end": v(-15, -92.25) * mm});
            skLineSegment(sketch, "E88.MirrorCS", {"start": v(-15, -92.25) * mm, "end": v(-15, -104.25) * mm});
            skArc(sketch, "E89.MirrorCS", {"start": v(15, -104.25) * mm, "mid": v(0, -119.25) * mm, "end": v(-15, -104.25) * mm});
            skCircle(sketch, "E90.MirrorC", {"center": v(0, -104.25) * mm, "radius": 6 * mm});
            skLineSegment(sketch, "E91.MirrorCS", {"start": v(15, -92.25) * mm, "end": v(15, -104.25) * mm});
            skLineSegment(sketch, "E92.MirrorCS", {"start": v(33, -74.25) * mm, "end": v(15, -92.25) * mm});
            skLineSegment(sketch, "E93.MirrorCS", {"start": v(0, -74.25) * mm, "end": v(0, -104.25) * mm, "construction": true});
            skSolve(sketch);
        }
        {
            var Q0;
            Q0=makeQuery(id+"F16.imprint","IMPRINT",FACE,{"disambiguationData":[TD([[makeQuery(id+"F16.imprint","IMPRINT",EDGE,{"derivedFrom":makeQuery(id+"F1.opExtrude","CAP_EDGE",EDGE,{"disambiguationData":[OSD([sQuery(id+"F0.wireOp",EDGE,"E1.left")])],"isStart":true})}),-1.0]])]});
            var Q1;
            {var subQ1=sQuery(id+"F16.wireOp",EDGE,"E80");Q1=makeQuery(id+"F16.imprint","IMPRINT",FACE,{"disambiguationData":[TD([[makeQuery(id+"F16.imprint","IMPRINT",EDGE,{"derivedFrom":subQ1}),-1.0]])]});}
            var Q2;
            {var subQ0=sQuery(id+"F16.wireOp",EDGE,"E87.MirrorCS");Q2=makeQuery(id+"F16.imprint","IMPRINT",FACE,{"disambiguationData":[TD([[makeQuery(id+"F16.imprint","IMPRINT",EDGE,{"derivedFrom":subQ0}),1.0]])]});}
            var Q3;
            Q3=makeQuery(id+"F2.opExtrude","CAP_FACE",FACE,{"disambiguationData":[OSD([sQuery(id+"F0.wireOp",EDGE,"E12"),sQuery(id+"F0.wireOp",EDGE,"E13"),sQuery(id+"F0.wireOp",EDGE,"E14"),sQuery(id+"F0.wireOp",EDGE,"E15"),sQuery(id+"F0.wireOp",EDGE,"E17.filletArc"),sQuery(id+"F0.wireOp",EDGE,"E18.filletArc"),sQuery(id+"F0.wireOp",EDGE,"E19.filletArc"),sQuery(id+"F0.wireOp",EDGE,"E20.filletArc"),sQuery(id+"F0.wireOp",EDGE,"E25.0"),sQuery(id+"F0.wireOp",EDGE,"E25.1"),sQuery(id+"F0.wireOp",EDGE,"E25.2"),sQuery(id+"F0.wireOp",EDGE,"E25.3"),sQuery(id+"F0.wireOp",EDGE,"E25.4"),sQuery(id+"F0.wireOp",EDGE,"E25.5"),sQuery(id+"F0.wireOp",EDGE,"E25.6"),sQuery(id+"F0.wireOp",EDGE,"E25.7")])],"isStart":false});
            extrude(context, id + "F17", {"entities" : qUnion([Q0, Q1, Q2]), "endBound" : BoundingType.UP_TO_SURFACE, "endBoundEntityFace" : qUnion([Q3]), "depth" : 25 * mm});
        }
    });
